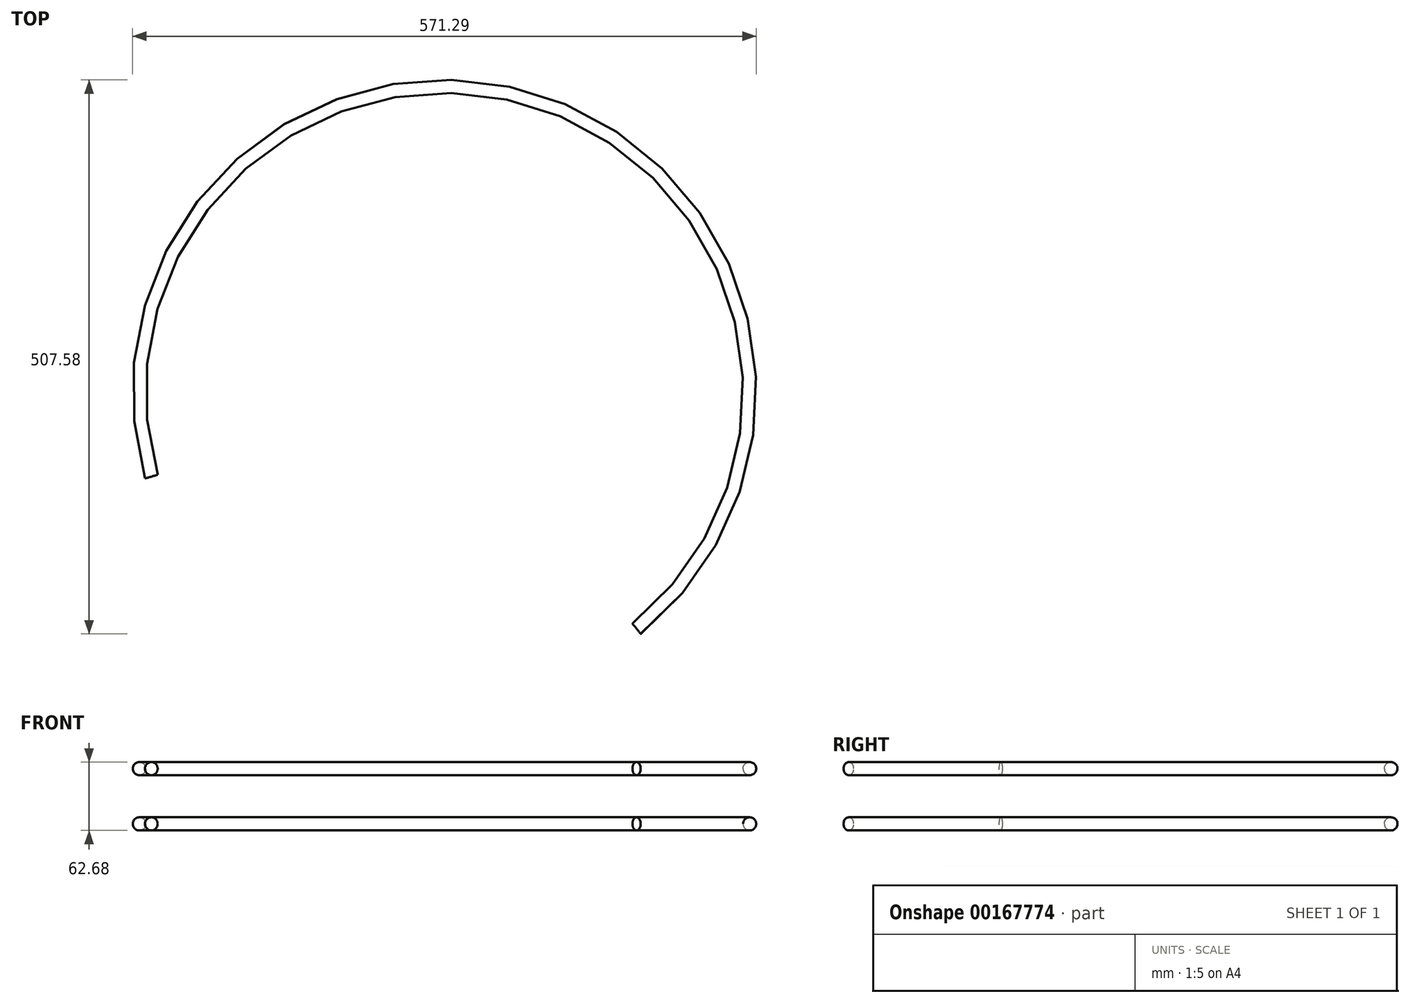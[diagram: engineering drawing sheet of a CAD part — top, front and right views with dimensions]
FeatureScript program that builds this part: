
annotation { "Feature Type Name" : "Feature", "Feature Type Description" : "" }
export const myFeature = defineFeature(function(context is Context, id is Id, definition is map)
    precondition{}
    {
        {
            var Q0;
            Q0=qCreatedBy(makeId("Top.planeOp"),FACE);
            var sketch = newSketch(context, id + "F0", { "sketchPlane" : qUnion([Q0])});
            skArc(sketch, "E0", {"start": v(113.66, -338.75) * mm, "mid": v(21.35, 144.95) * mm, "end": v(-330.57, -199.48) * mm});
            skSolve(sketch);
        }
        {
            var Q0;
            Q0=qCreatedBy(makeId("Top.planeOp"),FACE);
            cPlane(context, id + "F1", {"entities" : qUnion([Q0]), "cplaneType" : CPlaneType.OFFSET, "offset" : 50.8 * mm, "width" : 152.4 * mm, "height" : 152.4 * mm});
        }
        {
            var Q0;
            Q0=qCreatedBy(id+"F1.planeOp",FACE);
            var sketch = newSketch(context, id + "F2", { "sketchPlane" : qUnion([Q0])});
            skArc(sketch, "E1", {"start": v(113.66, -338.75) * mm, "mid": v(21.35, 144.95) * mm, "end": v(-330.57, -199.48) * mm});
            skSolve(sketch);
        }
        {
            var Q0;
            Q0=sQuery(id+"F2.wireOp",VERTEX,"E1.end");
            var Q1;
            Q1=sQuery(id+"F2.wireOp",VERTEX,"E1.center");
            var Q2;
            Q2=sQuery(id+"F0.wireOp",VERTEX,"E0.end");
            cPlane(context, id + "F3", {"entities" : qUnion([Q0, Q1, Q2]), "cplaneType" : CPlaneType.THREE_POINT, "offset" : 25.4 * mm, "width" : 152.4 * mm, "height" : 152.4 * mm});
        }
        {
            var Q0;
            Q0=qCreatedBy(id+"F3.planeOp",FACE);
            var sketch = newSketch(context, id + "F4", { "sketchPlane" : qUnion([Q0])});
            skCircle(sketch, "E2", {"center": v(-373.26, 50.62) * mm, "radius": 6.03 * mm});
            skSolve(sketch);
        }
        {
            var Q0;
            Q0=makeQuery(id+"F4.imprint","IMPRINT",FACE,{"disambiguationData":[TD([[makeQuery(id+"F4.imprint","IMPRINT",EDGE,{"derivedFrom":sQuery(id+"F4.wireOp",EDGE,"E2")}),1.0]])]});
            var Q1;
            Q1=sQuery(id+"F2.wireOp",EDGE,"E1");
            sweep(context, id + "F5", {"profiles" : qUnion([Q0]), "path" : qUnion([Q1])});
        }
        {
            var Q0;
            Q0=qCreatedBy(id+"F3.planeOp",FACE);
            var sketch = newSketch(context, id + "F6", { "sketchPlane" : qUnion([Q0])});
            skCircle(sketch, "E3", {"center": v(-373.26, 0) * mm, "radius": 6.03 * mm});
            skSolve(sketch);
        }
        {
            var Q0;
            Q0=makeQuery(id+"F6.imprint","IMPRINT",FACE,{"disambiguationData":[TD([[makeQuery(id+"F6.imprint","IMPRINT",EDGE,{"derivedFrom":sQuery(id+"F6.wireOp",EDGE,"E3")}),1.0]])]});
            var Q1;
            Q1=sQuery(id+"F0.wireOp",EDGE,"E0");
            sweep(context, id + "F7", {"profiles" : qUnion([Q0]), "path" : qUnion([Q1])});
        }
    });
